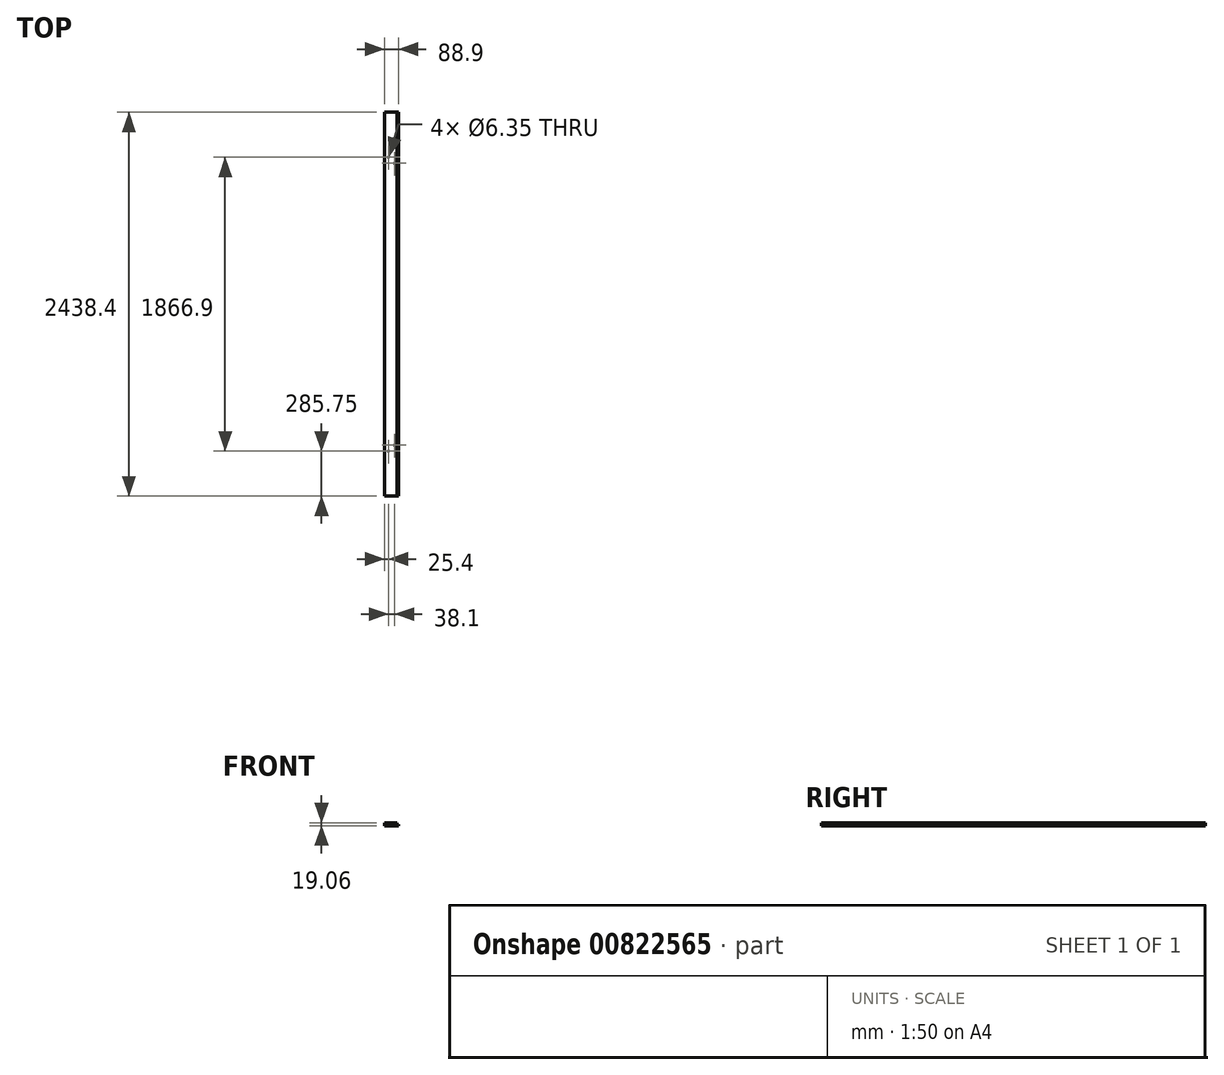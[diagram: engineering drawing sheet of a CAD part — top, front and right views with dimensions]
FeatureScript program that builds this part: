
annotation { "Feature Type Name" : "Feature", "Feature Type Description" : "" }
export const myFeature = defineFeature(function(context is Context, id is Id, definition is map)
    precondition{}
    {
        {
            var Q0;
            Q0=qCreatedBy(makeId("Front.planeOp"),FACE);
            var sketch = newSketch(context, id + "F0", { "sketchPlane" : qUnion([Q0])});
            skLineSegment(sketch, "E0.bottom", {"start": v(-44.45, 9.52) * mm, "end": v(44.45, 9.52) * mm});
            skLineSegment(sketch, "E0.top", {"start": v(-44.45, -9.52) * mm, "end": v(44.45, -9.52) * mm});
            skLineSegment(sketch, "E0.left", {"start": v(-44.45, 9.52) * mm, "end": v(-44.45, -9.53) * mm});
            skLineSegment(sketch, "E0.right", {"start": v(44.45, 9.52) * mm, "end": v(44.45, -9.53) * mm});
            skLineSegment(sketch, "E1", {"start": v(-44.45, -9.53) * mm, "end": v(44.45, 9.53) * mm, "construction": true});
            skSolve(sketch);
        }
        {
            var Q0;
            Q0=qSketchRegion(id+"F0",true);
            extrude(context, id + "F1", {"entities" : qUnion([Q0]), "endBound" : BoundingType.SYMMETRIC, "depth" : 2438.4 * mm, "offsetDistance" : 25.4 * mm});
        }
        {
            var Q0;
            Q0=makeQuery(id+"F1.opExtrude","CAP_FACE",FACE,{"disambiguationData":[OSD([sQuery(id+"F0.wireOp",EDGE,"E0.bottom"),sQuery(id+"F0.wireOp",EDGE,"E0.top"),sQuery(id+"F0.wireOp",EDGE,"E0.left"),sQuery(id+"F0.wireOp",EDGE,"E0.right")])],"isStart":false});
            var sketch = newSketch(context, id + "F2", { "sketchPlane" : qUnion([Q0])});
            skLineSegment(sketch, "E2.bottom", {"start": v(34.93, 22) * mm, "end": v(79.08, 22) * mm});
            skLineSegment(sketch, "E2.top", {"start": v(34.93, 0) * mm, "end": v(79.08, 0) * mm});
            skLineSegment(sketch, "E2.left", {"start": v(34.93, 22) * mm, "end": v(34.93, 0) * mm});
            skLineSegment(sketch, "E2.right", {"start": v(79.08, 22) * mm, "end": v(79.08, 0) * mm});
            skSolve(sketch);
        }
        {
            var Q0;
            Q0=qSketchRegion(id+"F2",true);
            extrude(context, id + "F3", {"entities" : qUnion([Q0]), "operationType" : NewBodyOperationType.REMOVE, "endBound" : BoundingType.THROUGH_ALL, "oppositeDirection" : true, "depth" : 25.4 * mm, "offsetDistance" : 25.4 * mm});
        }
        {
            var Q0;
            Q0=makeQuery(id+"F1.opExtrude","SWEPT_FACE",FACE,{"disambiguationData":[OSD([sQuery(id+"F0.wireOp",EDGE,"E0.bottom")])]});
            var sketch = newSketch(context, id + "F4", { "sketchPlane" : qUnion([Q0])});
            skLineSegment(sketch, "E3", {"start": v(6.28, -12.65) * mm, "end": v(0, -385.82) * mm});
            skLineSegment(sketch, "E4", {"start": v(-33.61, -385.82) * mm, "end": v(16.98, -401.5) * mm});
            skSolve(sketch);
        }
        {
            var Q0;
            {var subQ0=sQuery(id+"F0.wireOp",EDGE,"E0.bottom");Q0=makeQuery(id+"F4.imprint","IMPRINT",FACE,{"disambiguationData":[TD([[makeQuery(id+"F4.imprint","IMPRINT",EDGE,{"derivedFrom":makeQuery(id+"F1.opExtrude","CAP_EDGE",EDGE,{"disambiguationData":[OSD([subQ0])],"isStart":true})}),-1.0]])]});}
            var sketch = newSketch(context, id + "F5", { "sketchPlane" : qUnion([Q0])});
            skLineSegment(sketch, "E5.bottom", {"start": v(-19.05, -895.35) * mm, "end": v(19.05, -895.35) * mm, "construction": true});
            skLineSegment(sketch, "E5.top", {"start": v(-19.05, -933.45) * mm, "end": v(19.05, -933.45) * mm, "construction": true});
            skLineSegment(sketch, "E5.left", {"start": v(-19.05, -895.35) * mm, "end": v(-19.05, -933.45) * mm, "construction": true});
            skLineSegment(sketch, "E5.right", {"start": v(19.05, -895.35) * mm, "end": v(19.05, -933.45) * mm, "construction": true});
            skLineSegment(sketch, "E6", {"start": v(0, 0) * mm, "end": v(0, -895.35) * mm, "construction": true});
            skLineSegment(sketch, "E7", {"start": v(0, 0) * mm, "end": v(78.34, 0) * mm, "construction": true});
            skCircle(sketch, "E8", {"center": v(19.05, -895.35) * mm, "radius": 3.18 * mm});
            skCircle(sketch, "E9", {"center": v(-19.05, -933.45) * mm, "radius": 3.18 * mm});
            skCircle(sketch, "E10.MirrorC", {"center": v(-19.05, 933.45) * mm, "radius": 3.18 * mm});
            skCircle(sketch, "E11.MirrorC", {"center": v(19.05, 895.35) * mm, "radius": 3.18 * mm});
            skSolve(sketch);
        }
        {
            var Q0;
            Q0=qSketchRegion(id+"F5",true);
            extrude(context, id + "F6", {"entities" : qUnion([Q0]), "operationType" : NewBodyOperationType.REMOVE, "endBound" : BoundingType.UP_TO_NEXT, "oppositeDirection" : true, "depth" : 25.4 * mm, "offsetDistance" : 25.4 * mm});
        }
    });
